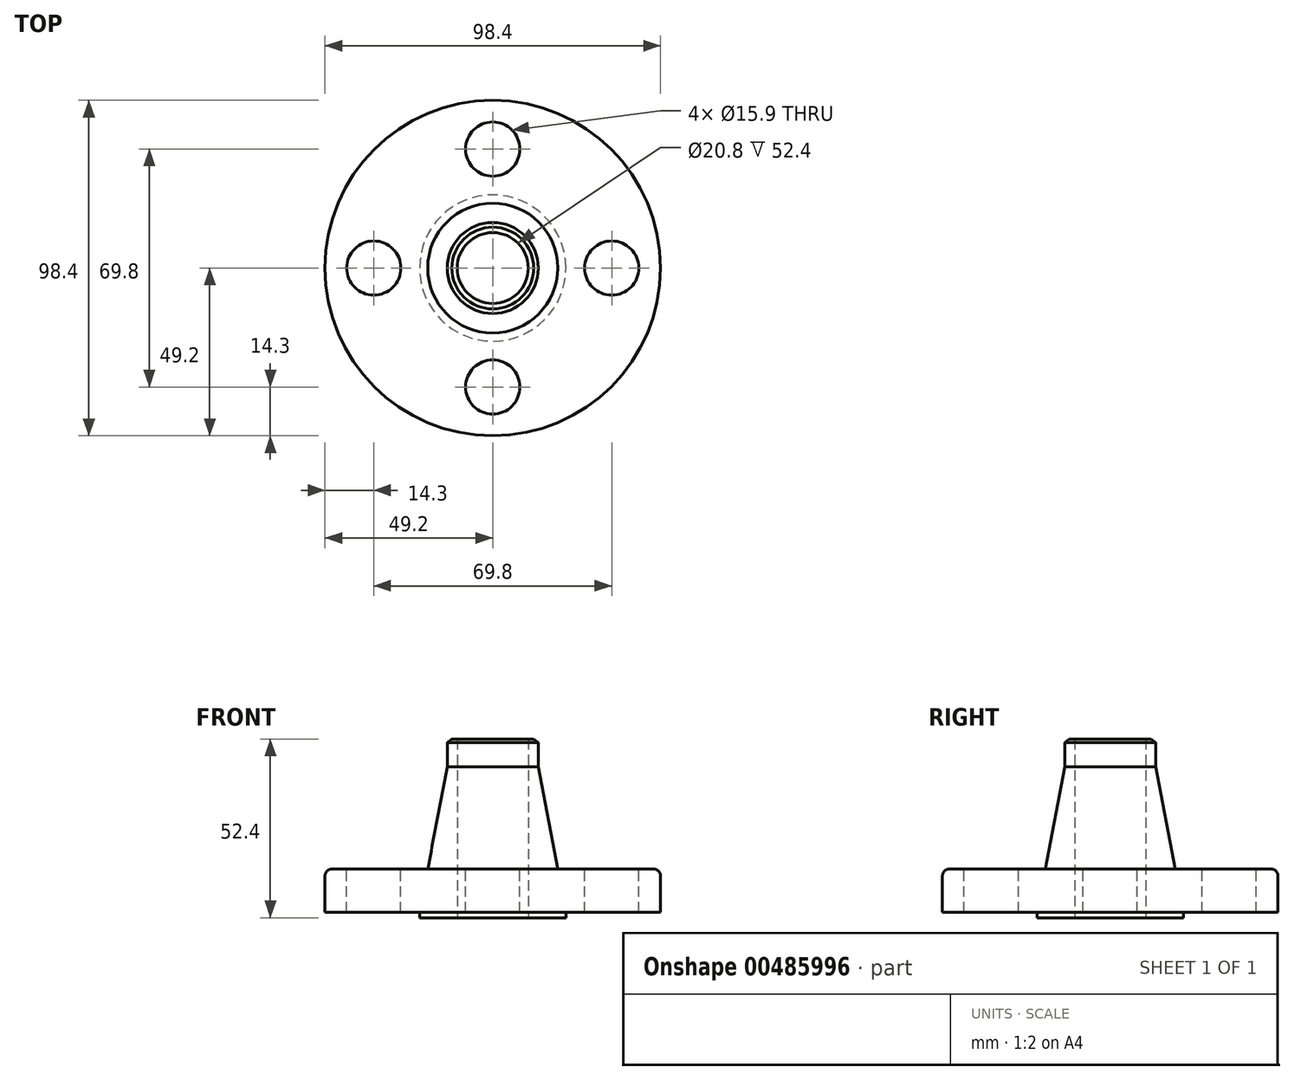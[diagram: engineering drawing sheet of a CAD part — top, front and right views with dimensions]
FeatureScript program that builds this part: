
annotation { "Feature Type Name" : "Feature", "Feature Type Description" : "" }
export const myFeature = defineFeature(function(context is Context, id is Id, definition is map)
    precondition{}
    {
        {
            var Q0;
            Q0=qCreatedBy(makeId("Front.planeOp"),FACE);
            var sketch = newSketch(context, id + "F0", { "sketchPlane" : qUnion([Q0])});
            skLineSegment(sketch, "E0", {"start": v(0, 0) * mm, "end": v(0, 52.4) * mm, "construction": true});
            skLineSegment(sketch, "E1", {"start": v(-10.4, 0) * mm, "end": v(-21.45, 0) * mm});
            skLineSegment(sketch, "E2", {"start": v(-21.45, 0) * mm, "end": v(-21.45, 1.6) * mm});
            skLineSegment(sketch, "E3", {"start": v(-21.45, 1.6) * mm, "end": v(-49.2, 1.6) * mm});
            skLineSegment(sketch, "E4", {"start": v(-49.2, 1.6) * mm, "end": v(-49.2, 12.3) * mm});
            skLineSegment(sketch, "E5", {"start": v(-12, 52.4) * mm, "end": v(-10.4, 52.4) * mm});
            skLineSegment(sketch, "E6", {"start": v(-10.4, 52.4) * mm, "end": v(-10.4, 0) * mm});
            skLineSegment(sketch, "E7", {"start": v(-47.2, 14.3) * mm, "end": v(-19.05, 14.3) * mm});
            skLineSegment(sketch, "E8", {"start": v(-19.05, 14.3) * mm, "end": v(-13.35, 44.3) * mm});
            skLineSegment(sketch, "E9", {"start": v(-13.35, 44.3) * mm, "end": v(-13.35, 51.36) * mm});
            skLineSegment(sketch, "E10", {"start": v(-13.35, 51.36) * mm, "end": v(-12, 52.4) * mm});
            skPoint(sketch, "E11.visualSharp", {"position": v(-49.2, 14.3) * mm});
            skArc(sketch, "E11.filletArc", {"start": v(-47.2, 14.3) * mm, "mid": v(-48.61, 13.71) * mm, "end": v(-49.2, 12.3) * mm});
            skSolve(sketch);
        }
        {
            var Q0;
            Q0=makeQuery(id+"F0.imprint","IMPRINT",FACE,{"disambiguationData":[TD([[makeQuery(id+"F0.imprint","IMPRINT",EDGE,{"derivedFrom":sQuery(id+"F0.wireOp",EDGE,"E1")}),-1.0]])]});
            var Q1;
            Q1=sQuery(id+"F0.wireOp",EDGE,"E0");
            revolve(context, id + "F1", {"entities" : qUnion([Q0]), "axis" : qUnion([Q1]), "revolveType" : RevolveType.FULL});
        }
        {
            var Q0;
            Q0=makeQuery(id+"F1.opRevolve","SWEPT_FACE",FACE,{"disambiguationData":[OSD([sQuery(id+"F0.wireOp",EDGE,"E7")])]});
            var sketch = newSketch(context, id + "F2", { "sketchPlane" : qUnion([Q0])});
            skCircle(sketch, "E12", {"center": v(0, 34.9) * mm, "radius": 7.95 * mm});
            skCircle(sketch, "E13.1.0", {"center": v(-34.9, 0) * mm, "radius": 7.95 * mm});
            skCircle(sketch, "E13.2.0", {"center": v(0, -34.9) * mm, "radius": 7.95 * mm});
            skPoint(sketch, "E13.center", {"position": v(0, 0) * mm});
            skCircle(sketch, "E14.1.3.0", {"center": v(34.9, 0) * mm, "radius": 7.95 * mm});
            skSolve(sketch);
        }
        {
            var Q0;
            Q0 = qSketchRegion(id + "F2", true);
            extrude(context, id + "F3", {"entities" : qUnion([Q0]), "operationType" : NewBodyOperationType.REMOVE, "endBound" : BoundingType.THROUGH_ALL, "oppositeDirection" : true, "depth" : 25 * mm});
        }
    });
